# Revit family: Storage-Teknion-LWBCT_Byward_Low_Cabinet_Top_Access-R2019
name_source: partatom
category: Furniture
units: mm (PartAtom-declared; Revit-internal decimal feet)

## family parameters
Always vertical = Yes
Cut with Voids When Loaded = No
OmniClass Number = 23.40.20.00
OmniClass Title = General Furniture and Specialties
Room Calculation Point = No
Shared = Yes
Work Plane-Based = No

## types (2) — shared parameters
Assembly Code = E2020200
Manufacturer = Teknion
Manufacturer Fax = 416.661.4586
Part Number = LWBCT
Product Documentation Link = https://assets.teknion.com
Product Line = Byward
Product Page URL = https://www.teknion.com
Series = Byward
Sustainability Data = https://www.teknion.com
URL = www.teknion.com
Unit Weight URL = http://www.teknion.com
Warranty = http://www.teknion.com

## per-type parameters (varying)
| type | Description | Model | Width |
| 21" Height, 14" Depth, 36" Width | Byward Low Cabinet, Top Access, 21" Height, 14" Depth, 36" Width | LWBCT211436 | 36 " |
| 21" Height, 14" Depth, 42" Width | Byward Low Cabinet, Top Access, 21" Height, 14" Depth, 42" Width | LWBCT211442 | 42 " |

## geometry (parser evidence)
native form markers: Sweep x2
no freeform markers — native parametric forms only
